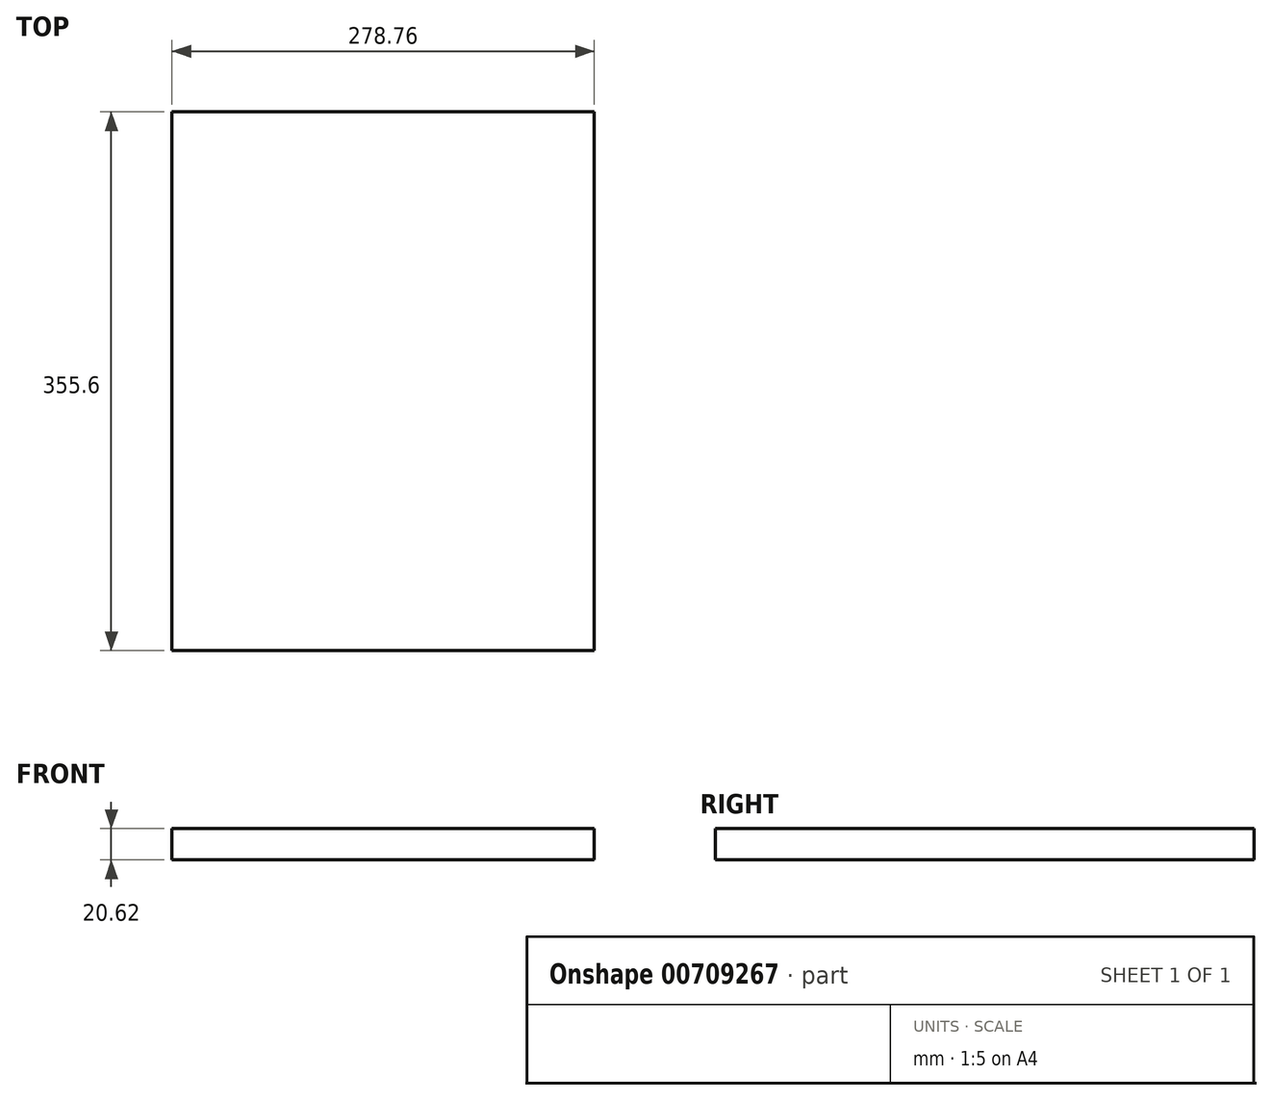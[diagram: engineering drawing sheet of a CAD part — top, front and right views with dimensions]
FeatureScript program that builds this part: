
annotation { "Feature Type Name" : "Feature", "Feature Type Description" : "" }
export const myFeature = defineFeature(function(context is Context, id is Id, definition is map)
    precondition{}
    {
        {
            var Q0;
            Q0=qCreatedBy(makeId("Front.planeOp"),FACE);
            var sketch = newSketch(context, id + "F0", { "sketchPlane" : qUnion([Q0])});
            skLineSegment(sketch, "E0.bottom", {"start": v(-139.38, -10.31) * mm, "end": v(139.38, -10.31) * mm});
            skLineSegment(sketch, "E0.top", {"start": v(-139.38, 10.31) * mm, "end": v(139.38, 10.31) * mm});
            skLineSegment(sketch, "E0.left", {"start": v(-139.38, 10.31) * mm, "end": v(-139.38, -10.31) * mm});
            skLineSegment(sketch, "E0.right", {"start": v(139.38, 10.31) * mm, "end": v(139.38, -10.31) * mm});
            skPoint(sketch, "E0.middle", {"position": v(0, 0) * mm});
            skSolve(sketch);
        }
        {
            var Q0;
            Q0 = qSketchRegion(id + "F0", true);
            extrude(context, id + "F1", {"entities" : qUnion([Q0]), "depth" : 355.6 * mm, "offsetDistance" : 25.4 * mm});
        }
    });
